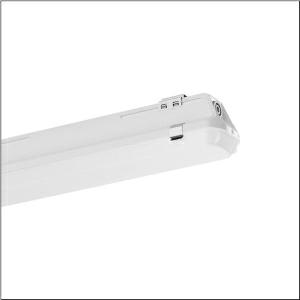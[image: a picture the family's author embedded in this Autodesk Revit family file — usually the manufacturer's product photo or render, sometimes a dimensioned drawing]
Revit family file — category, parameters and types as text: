
# Revit family: monsun_r__11_51fp208p460h_1e38
name_source: partatom
category: Lighting Fixtures
units: mm (PartAtom-declared; Revit-internal decimal feet)

## family parameters
Cut with Voids When Loaded = No
Host = Face
Light Source = No
Part Type = Normal
Room Calculation Point = No
Round Connector Dimension = Use Diameter
Shared = No

## types (1)
- Monsun® 11 (1 x LED, 5490 lm, 33.9 W, 4000K)
    Apparent Load = 34 VA
    CIE Flux Codes = 45 75 93 94 100
    Color Rendering = 80
    Color Temperature = 4000K
    Default Elevation = 1800 mm
    Description = Monsun® 11, damp-proof luminaire, chain hanger, primary optical cover: enclosure, of PC, light emission: direct distribution, primary light characteristic: symmetric, installation type: suspended mounting, surface-mounted, horizontal mounting, vertical mounting, LED, rated luminous flux: 5.490lm, luminous efficacy: 162lm/W, light colour: 840, colour temperature: 4000K, control gear: ECG, with terminal, 3-pole, max. 2.5mm², mains connection: 220..240V, AC, 50/60Hz, rated input power: 34W, luminaire housing, of glass-fibre reinforced polyester, uncoated, bright grey, incl. chain hanger, length: 1.590mm, width: 90mm, height: 88mm, clip for enclosure, of stainless steel (V2A), ceiling mounting element, of stainless steel (V2A), chain hanger, of stainless steel (V2A), protection rating (complete): IP66, insulation class (complete): insulation class I (protective earthing), certification: CE, ENEC, VDE, UKCA, protection symbol: D, impact resistance: IK08, permissible operating ambient temperature: -35..+40°C, standard: EN 50419, EN 60598-2-1, no direct snow, no direct sun, no direct rain, for indoor or canopied outdoor use, corresponds to IFS (International Featured Standards) requirements for safety and quality in the food industry, contact your sales advisor before using the luminaires in applications with unclear chemical exposure, large temperature fluctuations or condensation-forming humidity, LABS conformity tested according to VDMA 24364:2018-05, packaging unit: 1 piece
    Height = 89 mm
    Lamp = 1 x LED
    Lamp Light Flux = 5490 lm
    Lamp Power = 33.9 W
    Lamp count = 1
    Length = 1590 mm
    Luminous efficacy = 162 lm/W
    Manufacturer = Siteco
    ModVariant = No
    Model = 51FP208P460H
    Mounting Place = Ceiling
    Mounting Type = Surface mounted
    Number of Poles = 1
    OnlyDefault = Yes
    Power Factor = 1
    Product Name = Monsun® 11
    Product group = damp-proof luminaire
    ProductGroupID = 301
    Protection Class = Protection class I
    Protection Degree = IP 66
    RLX_Detail_Level = 1
    RLX_Emergency_Light_Flux = 0 lm
    RLX_Emergency_Type = 0
    RLX_Emergency_Type_DB = No
    RlxData = <blob elided: 88541 chars, md5=43c1a341>
    Socket = socket
    Standby Power = 0 W
    System Light Flux = 5490 lm
    System Power = 34 W
    Type Comments = Product without accessories
    Type Image = l_1004748.jpg
    URL = http://relux.com
    VarID = ---
    Voltage = 0 V
    Weight = 0.00 kg
    Width = 90 mm

## geometry (parser evidence)
native form markers: Blend x4, Sweep x12
no freeform markers — native parametric forms only
